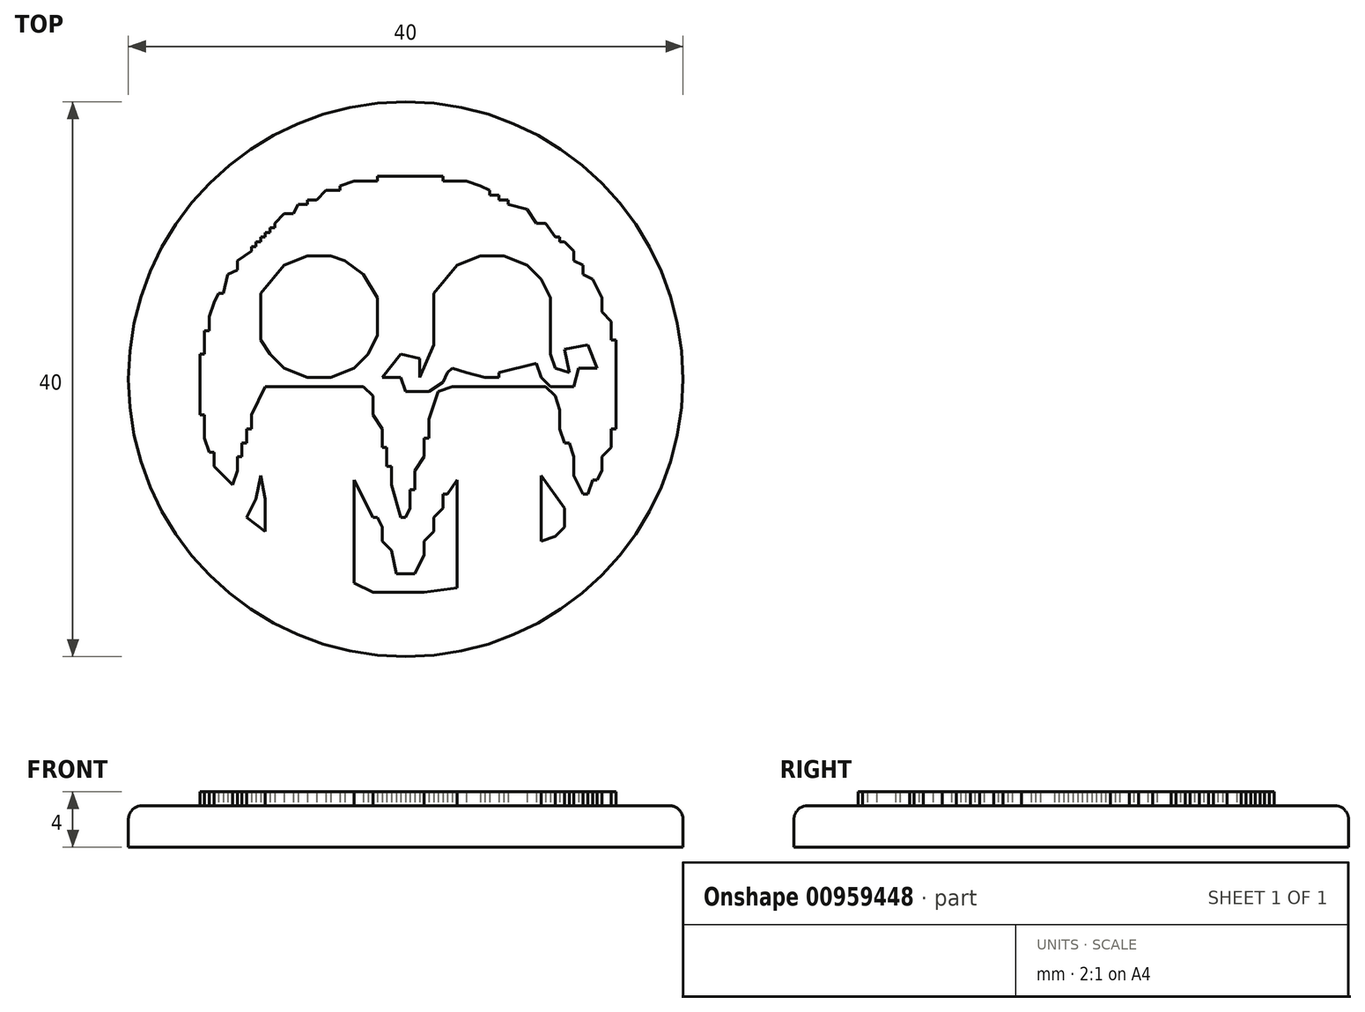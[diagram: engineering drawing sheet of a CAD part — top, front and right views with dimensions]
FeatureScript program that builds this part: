
annotation { "Feature Type Name" : "Feature", "Feature Type Description" : "" }
export const myFeature = defineFeature(function(context is Context, id is Id, definition is map)
    precondition{}
    {
        {
            var Q0;
            Q0=qCreatedBy(makeId("Front.planeOp"),FACE);
            var sketch = newSketch(context, id + "F0", { "sketchPlane" : qUnion([Q0])});
            skLineSegment(sketch, "E0.bottom", {"start": v(-20, 0) * mm, "end": v(0, 0) * mm});
            skLineSegment(sketch, "E0.top", {"start": v(-20, 3) * mm, "end": v(0, 3) * mm});
            skLineSegment(sketch, "E0.left", {"start": v(-20, 0) * mm, "end": v(-20, 3) * mm});
            skLineSegment(sketch, "E0.right", {"start": v(0, 0) * mm, "end": v(0, 3) * mm});
            skSolve(sketch);
        }
        {
            var Q0;
            Q0 = qSketchRegion(id + "F0", true);
            var Q1;
            Q1=sQuery(id+"F0.wireOp",EDGE,"E0.right");
            revolve(context, id + "F1", {"surfaceOperationType" : NewSurfaceOperationType.NEW, "entities" : qUnion([Q0]), "axis" : qUnion([Q1]), "revolveType" : RevolveType.FULL});
        }
        {
            var Q0;
            Q0=qCreatedBy(makeId("Top.planeOp"),FACE);
            cPlane(context, id + "F2", {"entities" : qUnion([Q0]), "cplaneType" : CPlaneType.OFFSET, "offset" : 3 * mm, "width" : 150 * mm, "height" : 150 * mm});
        }
        {
            var Q0;
            Q0=qCreatedBy(id+"F2.planeOp",FACE);
            var sketch = newSketch(context, id + "F3", { "sketchPlane" : qUnion([Q0])});
            skLineSegment(sketch, "E1", {"start": v(-2.03, 14.62) * mm, "end": v(-2.03, 14.29) * mm});
            skLineSegment(sketch, "E2", {"start": v(-2.03, 14.29) * mm, "end": v(-3.72, 14.29) * mm});
            skLineSegment(sketch, "E3", {"start": v(-3.72, 14.29) * mm, "end": v(-4.73, 13.95) * mm});
            skLineSegment(sketch, "E4", {"start": v(-4.73, 13.95) * mm, "end": v(-4.73, 13.61) * mm});
            skLineSegment(sketch, "E5", {"start": v(-4.73, 13.61) * mm, "end": v(-5.74, 13.61) * mm});
            skLineSegment(sketch, "E6", {"start": v(-5.74, 13.61) * mm, "end": v(-6.42, 12.94) * mm});
            skLineSegment(sketch, "E7", {"start": v(-6.42, 12.94) * mm, "end": v(-7.09, 12.94) * mm});
            skLineSegment(sketch, "E8", {"start": v(-7.09, 12.94) * mm, "end": v(-7.09, 12.6) * mm});
            skLineSegment(sketch, "E9", {"start": v(-7.09, 12.6) * mm, "end": v(-7.76, 12.6) * mm});
            skLineSegment(sketch, "E10", {"start": v(-7.76, 12.6) * mm, "end": v(-8.1, 11.93) * mm});
            skLineSegment(sketch, "E11", {"start": v(-8.1, 11.93) * mm, "end": v(-8.78, 11.93) * mm});
            skLineSegment(sketch, "E12", {"start": v(-8.78, 11.93) * mm, "end": v(-9.45, 11.25) * mm});
            skLineSegment(sketch, "E13", {"start": v(-9.45, 11.25) * mm, "end": v(-9.45, 10.92) * mm});
            skLineSegment(sketch, "E14", {"start": v(-9.45, 10.92) * mm, "end": v(-9.79, 10.92) * mm});
            skLineSegment(sketch, "E15", {"start": v(-9.79, 10.92) * mm, "end": v(-9.79, 10.58) * mm});
            skLineSegment(sketch, "E16", {"start": v(-9.79, 10.58) * mm, "end": v(-10.12, 10.58) * mm});
            skLineSegment(sketch, "E17", {"start": v(-10.12, 10.58) * mm, "end": v(-10.12, 10.24) * mm});
            skLineSegment(sketch, "E18", {"start": v(-10.12, 10.24) * mm, "end": v(-10.46, 10.24) * mm});
            skLineSegment(sketch, "E19", {"start": v(-10.46, 10.24) * mm, "end": v(-10.46, 9.9) * mm});
            skLineSegment(sketch, "E20", {"start": v(-10.46, 9.9) * mm, "end": v(-10.8, 9.9) * mm});
            skLineSegment(sketch, "E21", {"start": v(-10.8, 9.9) * mm, "end": v(-10.8, 9.57) * mm});
            skLineSegment(sketch, "E22", {"start": v(-10.8, 9.57) * mm, "end": v(-11.13, 9.57) * mm});
            skLineSegment(sketch, "E23", {"start": v(-11.13, 9.57) * mm, "end": v(-11.13, 9.23) * mm});
            skLineSegment(sketch, "E24", {"start": v(-11.13, 9.23) * mm, "end": v(-12.15, 8.56) * mm});
            skLineSegment(sketch, "E25", {"start": v(-12.15, 8.56) * mm, "end": v(-12.15, 7.88) * mm});
            skLineSegment(sketch, "E26", {"start": v(-12.15, 7.88) * mm, "end": v(-12.82, 7.54) * mm});
            skLineSegment(sketch, "E27", {"start": v(-12.82, 7.54) * mm, "end": v(-13.16, 6.2) * mm});
            skLineSegment(sketch, "E28", {"start": v(-13.16, 6.2) * mm, "end": v(-13.5, 6.2) * mm});
            skLineSegment(sketch, "E29", {"start": v(-13.5, 6.2) * mm, "end": v(-13.83, 5.52) * mm});
            skLineSegment(sketch, "E30", {"start": v(-13.83, 5.52) * mm, "end": v(-14.17, 4.51) * mm});
            skLineSegment(sketch, "E31", {"start": v(-14.17, 4.51) * mm, "end": v(-14.17, 3.5) * mm});
            skLineSegment(sketch, "E32", {"start": v(-14.17, 3.5) * mm, "end": v(-14.5, 3.5) * mm});
            skLineSegment(sketch, "E33", {"start": v(-14.5, 3.5) * mm, "end": v(-14.5, 1.81) * mm});
            skLineSegment(sketch, "E34", {"start": v(-14.5, 1.81) * mm, "end": v(-14.84, 1.81) * mm});
            skLineSegment(sketch, "E35", {"start": v(-14.84, 1.81) * mm, "end": v(-14.84, 0.8) * mm});
            skLineSegment(sketch, "E36", {"start": v(-14.84, 0.8) * mm, "end": v(-14.84, -2.57) * mm});
            skLineSegment(sketch, "E37", {"start": v(-14.84, -2.57) * mm, "end": v(-14.5, -2.57) * mm});
            skLineSegment(sketch, "E38", {"start": v(-14.5, -2.57) * mm, "end": v(-14.5, -4.25) * mm});
            skLineSegment(sketch, "E39", {"start": v(-14.5, -4.25) * mm, "end": v(-14.17, -5.26) * mm});
            skLineSegment(sketch, "E40", {"start": v(-14.17, -5.26) * mm, "end": v(-13.83, -5.26) * mm});
            skLineSegment(sketch, "E41", {"start": v(-13.83, -5.26) * mm, "end": v(-13.83, -6.28) * mm});
            skLineSegment(sketch, "E42", {"start": v(-13.83, -6.28) * mm, "end": v(-12.48, -7.62) * mm});
            skLineSegment(sketch, "E43", {"start": v(-12.48, -7.62) * mm, "end": v(-12.15, -6.61) * mm});
            skLineSegment(sketch, "E44", {"start": v(-12.15, -6.61) * mm, "end": v(-12.15, -5.6) * mm});
            skLineSegment(sketch, "E45", {"start": v(-12.15, -5.6) * mm, "end": v(-11.8, -5.6) * mm});
            skLineSegment(sketch, "E46", {"start": v(-11.8, -5.6) * mm, "end": v(-11.8, -4.59) * mm});
            skLineSegment(sketch, "E47", {"start": v(-11.8, -4.59) * mm, "end": v(-11.47, -4.59) * mm});
            skLineSegment(sketch, "E48", {"start": v(-11.47, -4.59) * mm, "end": v(-11.47, -3.58) * mm});
            skLineSegment(sketch, "E49", {"start": v(-11.47, -3.58) * mm, "end": v(-11.13, -3.58) * mm});
            skLineSegment(sketch, "E50", {"start": v(-11.13, -3.58) * mm, "end": v(-11.13, -2.57) * mm});
            skLineSegment(sketch, "E51", {"start": v(-11.13, -2.57) * mm, "end": v(-10.12, -0.55) * mm});
            skLineSegment(sketch, "E52", {"start": v(-10.12, -0.55) * mm, "end": v(-8.78, -0.55) * mm});
            skLineSegment(sketch, "E53", {"start": v(-8.78, -0.55) * mm, "end": v(-8.44, -0.55) * mm});
            skLineSegment(sketch, "E54", {"start": v(-8.44, -0.55) * mm, "end": v(-8.1, -0.55) * mm});
            skLineSegment(sketch, "E55", {"start": v(-8.1, -0.55) * mm, "end": v(-7.76, -0.55) * mm});
            skLineSegment(sketch, "E56", {"start": v(-7.76, -0.55) * mm, "end": v(-7.43, -0.55) * mm});
            skLineSegment(sketch, "E57", {"start": v(-7.43, -0.55) * mm, "end": v(-7.09, -0.55) * mm});
            skLineSegment(sketch, "E58", {"start": v(-7.09, -0.55) * mm, "end": v(-6.75, -0.55) * mm});
            skLineSegment(sketch, "E59", {"start": v(-6.75, -0.55) * mm, "end": v(-6.42, -0.55) * mm});
            skLineSegment(sketch, "E60", {"start": v(-6.42, -0.55) * mm, "end": v(-6.08, -0.55) * mm});
            skLineSegment(sketch, "E61", {"start": v(-6.08, -0.55) * mm, "end": v(-5.74, -0.55) * mm});
            skLineSegment(sketch, "E62", {"start": v(-5.74, -0.55) * mm, "end": v(-5.4, -0.55) * mm});
            skLineSegment(sketch, "E63", {"start": v(-5.4, -0.55) * mm, "end": v(-5.07, -0.55) * mm});
            skLineSegment(sketch, "E64", {"start": v(-5.07, -0.55) * mm, "end": v(-3.04, -0.55) * mm});
            skLineSegment(sketch, "E65", {"start": v(-3.04, -0.55) * mm, "end": v(-2.37, -1.22) * mm});
            skLineSegment(sketch, "E66", {"start": v(-2.37, -1.22) * mm, "end": v(-2.37, -2.57) * mm});
            skLineSegment(sketch, "E67", {"start": v(-2.37, -2.57) * mm, "end": v(-1.7, -3.58) * mm});
            skLineSegment(sketch, "E68", {"start": v(-1.7, -3.58) * mm, "end": v(-1.7, -4.93) * mm});
            skLineSegment(sketch, "E69", {"start": v(-1.7, -4.93) * mm, "end": v(-1.36, -4.93) * mm});
            skLineSegment(sketch, "E70", {"start": v(-1.36, -4.93) * mm, "end": v(-1.36, -6.28) * mm});
            skLineSegment(sketch, "E71", {"start": v(-1.36, -6.28) * mm, "end": v(-1.02, -6.28) * mm});
            skLineSegment(sketch, "E72", {"start": v(-1.02, -6.28) * mm, "end": v(-1.02, -7.62) * mm});
            skLineSegment(sketch, "E73", {"start": v(-1.02, -7.62) * mm, "end": v(-0.35, -9.98) * mm});
            skLineSegment(sketch, "E74", {"start": v(-0.35, -9.98) * mm, "end": v(-0.01, -9.98) * mm});
            skLineSegment(sketch, "E75", {"start": v(-0.01, -9.98) * mm, "end": v(0.33, -9.3) * mm});
            skLineSegment(sketch, "E76", {"start": v(0.33, -9.3) * mm, "end": v(0.33, -7.96) * mm});
            skLineSegment(sketch, "E77", {"start": v(0.33, -7.96) * mm, "end": v(0.66, -7.96) * mm});
            skLineSegment(sketch, "E78", {"start": v(0.66, -7.96) * mm, "end": v(0.66, -6.61) * mm});
            skLineSegment(sketch, "E79", {"start": v(0.66, -6.61) * mm, "end": v(1.34, -5.6) * mm});
            skLineSegment(sketch, "E80", {"start": v(1.34, -5.6) * mm, "end": v(1.34, -4.25) * mm});
            skLineSegment(sketch, "E81", {"start": v(1.34, -4.25) * mm, "end": v(1.67, -4.25) * mm});
            skLineSegment(sketch, "E82", {"start": v(1.67, -4.25) * mm, "end": v(1.67, -2.9) * mm});
            skLineSegment(sketch, "E83", {"start": v(1.67, -2.9) * mm, "end": v(2.35, -0.88) * mm});
            skLineSegment(sketch, "E84", {"start": v(2.35, -0.88) * mm, "end": v(3.36, -0.55) * mm});
            skLineSegment(sketch, "E85", {"start": v(3.36, -0.55) * mm, "end": v(4.7, -0.55) * mm});
            skLineSegment(sketch, "E86", {"start": v(4.7, -0.55) * mm, "end": v(5.04, -0.55) * mm});
            skLineSegment(sketch, "E87", {"start": v(5.04, -0.55) * mm, "end": v(5.38, -0.55) * mm});
            skLineSegment(sketch, "E88", {"start": v(5.38, -0.55) * mm, "end": v(5.72, -0.55) * mm});
            skLineSegment(sketch, "E89", {"start": v(5.72, -0.55) * mm, "end": v(6.06, -0.55) * mm});
            skLineSegment(sketch, "E90", {"start": v(6.06, -0.55) * mm, "end": v(6.4, -0.55) * mm});
            skLineSegment(sketch, "E91", {"start": v(6.4, -0.55) * mm, "end": v(6.73, -0.55) * mm});
            skLineSegment(sketch, "E92", {"start": v(6.73, -0.55) * mm, "end": v(7.07, -0.55) * mm});
            skLineSegment(sketch, "E93", {"start": v(7.07, -0.55) * mm, "end": v(7.4, -0.55) * mm});
            skLineSegment(sketch, "E94", {"start": v(7.4, -0.55) * mm, "end": v(7.74, -0.55) * mm});
            skLineSegment(sketch, "E95", {"start": v(7.74, -0.55) * mm, "end": v(8.08, -0.55) * mm});
            skLineSegment(sketch, "E96", {"start": v(8.08, -0.55) * mm, "end": v(8.42, -0.55) * mm});
            skLineSegment(sketch, "E97", {"start": v(8.42, -0.55) * mm, "end": v(10.1, -0.55) * mm});
            skLineSegment(sketch, "E98", {"start": v(10.1, -0.55) * mm, "end": v(10.78, -1.22) * mm});
            skLineSegment(sketch, "E99", {"start": v(10.78, -1.22) * mm, "end": v(11.11, -2.23) * mm});
            skLineSegment(sketch, "E100", {"start": v(11.11, -2.23) * mm, "end": v(11.11, -3.58) * mm});
            skLineSegment(sketch, "E101", {"start": v(11.11, -3.58) * mm, "end": v(11.45, -4.59) * mm});
            skLineSegment(sketch, "E102", {"start": v(11.45, -4.59) * mm, "end": v(11.79, -4.59) * mm});
            skLineSegment(sketch, "E103", {"start": v(11.79, -4.59) * mm, "end": v(12.12, -5.6) * mm});
            skLineSegment(sketch, "E104", {"start": v(12.12, -5.6) * mm, "end": v(12.12, -6.95) * mm});
            skLineSegment(sketch, "E105", {"start": v(12.12, -6.95) * mm, "end": v(12.8, -8.3) * mm});
            skLineSegment(sketch, "E106", {"start": v(12.8, -8.3) * mm, "end": v(13.13, -8.3) * mm});
            skLineSegment(sketch, "E107", {"start": v(13.13, -8.3) * mm, "end": v(13.47, -7.29) * mm});
            skLineSegment(sketch, "E108", {"start": v(13.47, -7.29) * mm, "end": v(13.8, -7.29) * mm});
            skLineSegment(sketch, "E109", {"start": v(13.8, -7.29) * mm, "end": v(14.15, -6.61) * mm});
            skLineSegment(sketch, "E110", {"start": v(14.15, -6.61) * mm, "end": v(14.15, -5.6) * mm});
            skLineSegment(sketch, "E111", {"start": v(14.15, -5.6) * mm, "end": v(14.82, -4.93) * mm});
            skLineSegment(sketch, "E112", {"start": v(14.82, -4.93) * mm, "end": v(14.82, -3.58) * mm});
            skLineSegment(sketch, "E113", {"start": v(14.82, -3.58) * mm, "end": v(15.16, -3.58) * mm});
            skLineSegment(sketch, "E114", {"start": v(15.16, -3.58) * mm, "end": v(15.16, -2.57) * mm});
            skLineSegment(sketch, "E115", {"start": v(15.16, -2.57) * mm, "end": v(15.16, -1.22) * mm});
            skLineSegment(sketch, "E116", {"start": v(15.16, -1.22) * mm, "end": v(15.16, -0.88) * mm});
            skLineSegment(sketch, "E117", {"start": v(15.16, -0.88) * mm, "end": v(15.16, -0.55) * mm});
            skLineSegment(sketch, "E118", {"start": v(15.16, -0.55) * mm, "end": v(15.16, -0.2) * mm});
            skLineSegment(sketch, "E119", {"start": v(15.16, -0.2) * mm, "end": v(15.16, 0.13) * mm});
            skLineSegment(sketch, "E120", {"start": v(15.16, 0.13) * mm, "end": v(15.16, 0.47) * mm});
            skLineSegment(sketch, "E121", {"start": v(15.16, 0.47) * mm, "end": v(15.16, 0.8) * mm});
            skLineSegment(sketch, "E122", {"start": v(15.16, 0.8) * mm, "end": v(15.16, 1.14) * mm});
            skLineSegment(sketch, "E123", {"start": v(15.16, 1.14) * mm, "end": v(15.16, 2.83) * mm});
            skLineSegment(sketch, "E124", {"start": v(15.16, 2.83) * mm, "end": v(14.82, 2.83) * mm});
            skLineSegment(sketch, "E125", {"start": v(14.82, 2.83) * mm, "end": v(14.82, 4.17) * mm});
            skLineSegment(sketch, "E126", {"start": v(14.82, 4.17) * mm, "end": v(14.15, 4.85) * mm});
            skLineSegment(sketch, "E127", {"start": v(14.15, 4.85) * mm, "end": v(14.15, 5.86) * mm});
            skLineSegment(sketch, "E128", {"start": v(14.15, 5.86) * mm, "end": v(13.47, 7.2) * mm});
            skLineSegment(sketch, "E129", {"start": v(13.47, 7.2) * mm, "end": v(12.8, 7.54) * mm});
            skLineSegment(sketch, "E130", {"start": v(12.8, 7.54) * mm, "end": v(12.8, 8.22) * mm});
            skLineSegment(sketch, "E131", {"start": v(12.8, 8.22) * mm, "end": v(12.12, 8.56) * mm});
            skLineSegment(sketch, "E132", {"start": v(12.12, 8.56) * mm, "end": v(12.12, 9.23) * mm});
            skLineSegment(sketch, "E133", {"start": v(12.12, 9.23) * mm, "end": v(11.45, 9.9) * mm});
            skLineSegment(sketch, "E134", {"start": v(11.45, 9.9) * mm, "end": v(11.11, 9.9) * mm});
            skLineSegment(sketch, "E135", {"start": v(11.11, 9.9) * mm, "end": v(11.11, 10.24) * mm});
            skLineSegment(sketch, "E136", {"start": v(11.11, 10.24) * mm, "end": v(10.78, 10.24) * mm});
            skLineSegment(sketch, "E137", {"start": v(10.78, 10.24) * mm, "end": v(10.1, 11.25) * mm});
            skLineSegment(sketch, "E138", {"start": v(10.1, 11.25) * mm, "end": v(9.43, 11.25) * mm});
            skLineSegment(sketch, "E139", {"start": v(9.43, 11.25) * mm, "end": v(8.75, 12.26) * mm});
            skLineSegment(sketch, "E140", {"start": v(8.75, 12.26) * mm, "end": v(7.4, 12.6) * mm});
            skLineSegment(sketch, "E141", {"start": v(7.4, 12.6) * mm, "end": v(7.4, 12.94) * mm});
            skLineSegment(sketch, "E142", {"start": v(7.4, 12.94) * mm, "end": v(6.73, 12.94) * mm});
            skLineSegment(sketch, "E143", {"start": v(6.73, 12.94) * mm, "end": v(6.73, 13.28) * mm});
            skLineSegment(sketch, "E144", {"start": v(6.73, 13.28) * mm, "end": v(6.06, 13.28) * mm});
            skLineSegment(sketch, "E145", {"start": v(6.06, 13.28) * mm, "end": v(6.06, 13.61) * mm});
            skLineSegment(sketch, "E146", {"start": v(6.06, 13.61) * mm, "end": v(5.38, 13.95) * mm});
            skLineSegment(sketch, "E147", {"start": v(5.38, 13.95) * mm, "end": v(4.37, 14.29) * mm});
            skLineSegment(sketch, "E148", {"start": v(4.37, 14.29) * mm, "end": v(2.69, 14.29) * mm});
            skLineSegment(sketch, "E149", {"start": v(2.69, 14.29) * mm, "end": v(2.69, 14.62) * mm});
            skLineSegment(sketch, "E150", {"start": v(2.69, 14.62) * mm, "end": v(1.67, 14.62) * mm});
            skLineSegment(sketch, "E151", {"start": v(1.67, 14.62) * mm, "end": v(0.33, 14.62) * mm});
            skLineSegment(sketch, "E152", {"start": v(0.33, 14.62) * mm, "end": v(-0.01, 14.62) * mm});
            skLineSegment(sketch, "E153", {"start": v(-0.01, 14.62) * mm, "end": v(-0.35, 14.62) * mm});
            skLineSegment(sketch, "E154", {"start": v(-0.35, 14.62) * mm, "end": v(-0.69, 14.62) * mm});
            skLineSegment(sketch, "E155", {"start": v(-0.69, 14.62) * mm, "end": v(-2.03, 14.62) * mm});
            skLineSegment(sketch, "E156", {"start": v(-7.09, 8.9) * mm, "end": v(-8.78, 8.22) * mm});
            skLineSegment(sketch, "E157", {"start": v(-8.78, 8.22) * mm, "end": v(-10.46, 6.2) * mm});
            skLineSegment(sketch, "E158", {"start": v(-10.46, 6.2) * mm, "end": v(-10.46, 2.83) * mm});
            skLineSegment(sketch, "E159", {"start": v(-10.46, 2.83) * mm, "end": v(-9.79, 1.81) * mm});
            skLineSegment(sketch, "E160", {"start": v(-9.79, 1.81) * mm, "end": v(-8.78, 0.8) * mm});
            skLineSegment(sketch, "E161", {"start": v(-8.78, 0.8) * mm, "end": v(-7.09, 0.13) * mm});
            skLineSegment(sketch, "E162", {"start": v(-7.09, 0.13) * mm, "end": v(-5.4, 0.13) * mm});
            skLineSegment(sketch, "E163", {"start": v(-5.4, 0.13) * mm, "end": v(-3.72, 0.8) * mm});
            skLineSegment(sketch, "E164", {"start": v(-3.72, 0.8) * mm, "end": v(-2.7, 1.81) * mm});
            skLineSegment(sketch, "E165", {"start": v(-2.7, 1.81) * mm, "end": v(-2.03, 3.16) * mm});
            skLineSegment(sketch, "E166", {"start": v(-2.03, 3.16) * mm, "end": v(-2.03, 5.86) * mm});
            skLineSegment(sketch, "E167", {"start": v(-2.03, 5.86) * mm, "end": v(-3.04, 7.54) * mm});
            skLineSegment(sketch, "E168", {"start": v(-3.04, 7.54) * mm, "end": v(-4.4, 8.56) * mm});
            skLineSegment(sketch, "E169", {"start": v(-4.4, 8.56) * mm, "end": v(-5.4, 8.9) * mm});
            skLineSegment(sketch, "E170", {"start": v(-5.4, 8.9) * mm, "end": v(-7.09, 8.9) * mm});
            skLineSegment(sketch, "E171", {"start": v(5.38, 8.9) * mm, "end": v(3.7, 8.22) * mm});
            skLineSegment(sketch, "E172", {"start": v(3.7, 8.22) * mm, "end": v(2.01, 6.2) * mm});
            skLineSegment(sketch, "E173", {"start": v(2.01, 6.2) * mm, "end": v(2.01, 4.85) * mm});
            skLineSegment(sketch, "E174", {"start": v(2.01, 4.85) * mm, "end": v(2.01, 4.51) * mm});
            skLineSegment(sketch, "E175", {"start": v(2.01, 4.51) * mm, "end": v(2.01, 4.17) * mm});
            skLineSegment(sketch, "E176", {"start": v(2.01, 4.17) * mm, "end": v(2.01, 3.84) * mm});
            skLineSegment(sketch, "E177", {"start": v(2.01, 3.84) * mm, "end": v(2.01, 3.5) * mm});
            skLineSegment(sketch, "E178", {"start": v(2.01, 3.5) * mm, "end": v(2.01, 3.16) * mm});
            skLineSegment(sketch, "E179", {"start": v(2.01, 3.16) * mm, "end": v(2.01, 2.83) * mm});
            skLineSegment(sketch, "E180", {"start": v(2.01, 2.83) * mm, "end": v(2.01, 2.49) * mm});
            skLineSegment(sketch, "E181", {"start": v(2.01, 2.49) * mm, "end": v(1, 0.13) * mm});
            skLineSegment(sketch, "E182", {"start": v(1, 0.13) * mm, "end": v(1, 1.48) * mm});
            skLineSegment(sketch, "E183", {"start": v(1, 1.48) * mm, "end": v(-0.35, 1.81) * mm});
            skLineSegment(sketch, "E184", {"start": v(-0.35, 1.81) * mm, "end": v(-1.7, 0.13) * mm});
            skLineSegment(sketch, "E185", {"start": v(-1.7, 0.13) * mm, "end": v(-0.35, 0.13) * mm});
            skLineSegment(sketch, "E186", {"start": v(-0.35, 0.13) * mm, "end": v(-0.01, -0.88) * mm});
            skLineSegment(sketch, "E187", {"start": v(-0.01, -0.88) * mm, "end": v(1.67, -0.88) * mm});
            skLineSegment(sketch, "E188", {"start": v(1.67, -0.88) * mm, "end": v(2.69, -0.2) * mm});
            skLineSegment(sketch, "E189", {"start": v(2.69, -0.2) * mm, "end": v(3.02, 0.47) * mm});
            skLineSegment(sketch, "E190", {"start": v(3.02, 0.47) * mm, "end": v(3.36, 0.8) * mm});
            skLineSegment(sketch, "E191", {"start": v(3.36, 0.8) * mm, "end": v(4.37, 0.47) * mm});
            skLineSegment(sketch, "E192", {"start": v(4.37, 0.47) * mm, "end": v(5.72, 0.13) * mm});
            skLineSegment(sketch, "E193", {"start": v(5.72, 0.13) * mm, "end": v(6.73, 0.13) * mm});
            skLineSegment(sketch, "E194", {"start": v(6.73, 0.13) * mm, "end": v(6.73, 0.47) * mm});
            skLineSegment(sketch, "E195", {"start": v(6.73, 0.47) * mm, "end": v(9.43, 1.14) * mm});
            skLineSegment(sketch, "E196", {"start": v(9.43, 1.14) * mm, "end": v(9.76, 0.13) * mm});
            skLineSegment(sketch, "E197", {"start": v(9.76, 0.13) * mm, "end": v(10.1, -0.2) * mm});
            skLineSegment(sketch, "E198", {"start": v(10.1, -0.2) * mm, "end": v(10.44, -0.55) * mm});
            skLineSegment(sketch, "E199", {"start": v(10.44, -0.55) * mm, "end": v(12.12, -0.55) * mm});
            skLineSegment(sketch, "E200", {"start": v(12.12, -0.55) * mm, "end": v(12.46, 0.8) * mm});
            skLineSegment(sketch, "E201", {"start": v(12.46, 0.8) * mm, "end": v(13.8, 0.8) * mm});
            skLineSegment(sketch, "E202", {"start": v(13.8, 0.8) * mm, "end": v(13.13, 2.49) * mm});
            skLineSegment(sketch, "E203", {"start": v(13.13, 2.49) * mm, "end": v(11.45, 2.15) * mm});
            skLineSegment(sketch, "E204", {"start": v(11.45, 2.15) * mm, "end": v(11.79, 0.47) * mm});
            skLineSegment(sketch, "E205", {"start": v(11.79, 0.47) * mm, "end": v(10.78, 0.8) * mm});
            skLineSegment(sketch, "E206", {"start": v(10.78, 0.8) * mm, "end": v(10.44, 1.81) * mm});
            skLineSegment(sketch, "E207", {"start": v(10.44, 1.81) * mm, "end": v(10.44, 3.16) * mm});
            skLineSegment(sketch, "E208", {"start": v(10.44, 3.16) * mm, "end": v(10.44, 3.5) * mm});
            skLineSegment(sketch, "E209", {"start": v(10.44, 3.5) * mm, "end": v(10.44, 3.84) * mm});
            skLineSegment(sketch, "E210", {"start": v(10.44, 3.84) * mm, "end": v(10.44, 4.17) * mm});
            skLineSegment(sketch, "E211", {"start": v(10.44, 4.17) * mm, "end": v(10.44, 5.86) * mm});
            skLineSegment(sketch, "E212", {"start": v(10.44, 5.86) * mm, "end": v(9.76, 7.2) * mm});
            skLineSegment(sketch, "E213", {"start": v(9.76, 7.2) * mm, "end": v(8.75, 8.22) * mm});
            skLineSegment(sketch, "E214", {"start": v(8.75, 8.22) * mm, "end": v(7.07, 8.9) * mm});
            skLineSegment(sketch, "E215", {"start": v(7.07, 8.9) * mm, "end": v(5.38, 8.9) * mm});
            skLineSegment(sketch, "E216", {"start": v(-10.46, -6.95) * mm, "end": v(-10.8, -8.63) * mm});
            skLineSegment(sketch, "E217", {"start": v(-10.8, -8.63) * mm, "end": v(-11.47, -9.98) * mm});
            skLineSegment(sketch, "E218", {"start": v(-11.47, -9.98) * mm, "end": v(-10.12, -11) * mm});
            skLineSegment(sketch, "E219", {"start": v(-10.12, -11) * mm, "end": v(-10.12, -9.65) * mm});
            skLineSegment(sketch, "E220", {"start": v(-10.12, -9.65) * mm, "end": v(-10.12, -9.3) * mm});
            skLineSegment(sketch, "E221", {"start": v(-10.12, -9.3) * mm, "end": v(-10.12, -8.97) * mm});
            skLineSegment(sketch, "E222", {"start": v(-10.12, -8.97) * mm, "end": v(-10.12, -8.63) * mm});
            skLineSegment(sketch, "E223", {"start": v(-10.12, -8.63) * mm, "end": v(-10.46, -6.95) * mm});
            skLineSegment(sketch, "E224", {"start": v(9.76, -6.95) * mm, "end": v(9.76, -8.3) * mm});
            skLineSegment(sketch, "E225", {"start": v(9.76, -8.3) * mm, "end": v(9.76, -8.63) * mm});
            skLineSegment(sketch, "E226", {"start": v(9.76, -8.63) * mm, "end": v(9.76, -8.97) * mm});
            skLineSegment(sketch, "E227", {"start": v(9.76, -8.97) * mm, "end": v(9.76, -9.3) * mm});
            skLineSegment(sketch, "E228", {"start": v(9.76, -9.3) * mm, "end": v(9.76, -11.67) * mm});
            skLineSegment(sketch, "E229", {"start": v(9.76, -11.67) * mm, "end": v(10.78, -11.33) * mm});
            skLineSegment(sketch, "E230", {"start": v(10.78, -11.33) * mm, "end": v(11.11, -11) * mm});
            skLineSegment(sketch, "E231", {"start": v(11.11, -11) * mm, "end": v(11.45, -10.66) * mm});
            skLineSegment(sketch, "E232", {"start": v(11.45, -10.66) * mm, "end": v(11.45, -9.3) * mm});
            skLineSegment(sketch, "E233", {"start": v(11.45, -9.3) * mm, "end": v(9.76, -6.95) * mm});
            skLineSegment(sketch, "E234", {"start": v(-3.72, -7.29) * mm, "end": v(-3.72, -8.63) * mm});
            skLineSegment(sketch, "E235", {"start": v(-3.72, -8.63) * mm, "end": v(-3.72, -8.97) * mm});
            skLineSegment(sketch, "E236", {"start": v(-3.72, -8.97) * mm, "end": v(-3.72, -9.3) * mm});
            skLineSegment(sketch, "E237", {"start": v(-3.72, -9.3) * mm, "end": v(-3.72, -9.65) * mm});
            skLineSegment(sketch, "E238", {"start": v(-3.72, -9.65) * mm, "end": v(-3.72, -9.98) * mm});
            skLineSegment(sketch, "E239", {"start": v(-3.72, -9.98) * mm, "end": v(-3.72, -10.32) * mm});
            skLineSegment(sketch, "E240", {"start": v(-3.72, -10.32) * mm, "end": v(-3.72, -10.66) * mm});
            skLineSegment(sketch, "E241", {"start": v(-3.72, -10.66) * mm, "end": v(-3.72, -11) * mm});
            skLineSegment(sketch, "E242", {"start": v(-3.72, -11) * mm, "end": v(-3.72, -11.33) * mm});
            skLineSegment(sketch, "E243", {"start": v(-3.72, -11.33) * mm, "end": v(-3.72, -11.67) * mm});
            skLineSegment(sketch, "E244", {"start": v(-3.72, -11.67) * mm, "end": v(-3.72, -12) * mm});
            skLineSegment(sketch, "E245", {"start": v(-3.72, -12) * mm, "end": v(-3.72, -12.34) * mm});
            skLineSegment(sketch, "E246", {"start": v(-3.72, -12.34) * mm, "end": v(-3.72, -14.7) * mm});
            skLineSegment(sketch, "E247", {"start": v(-3.72, -14.7) * mm, "end": v(-2.37, -15.38) * mm});
            skLineSegment(sketch, "E248", {"start": v(-2.37, -15.38) * mm, "end": v(-1.02, -15.38) * mm});
            skLineSegment(sketch, "E249", {"start": v(-1.02, -15.38) * mm, "end": v(-0.69, -15.38) * mm});
            skLineSegment(sketch, "E250", {"start": v(-0.69, -15.38) * mm, "end": v(-0.35, -15.38) * mm});
            skLineSegment(sketch, "E251", {"start": v(-0.35, -15.38) * mm, "end": v(-0.01, -15.38) * mm});
            skLineSegment(sketch, "E252", {"start": v(-0.01, -15.38) * mm, "end": v(0.33, -15.38) * mm});
            skLineSegment(sketch, "E253", {"start": v(0.33, -15.38) * mm, "end": v(0.66, -15.38) * mm});
            skLineSegment(sketch, "E254", {"start": v(0.66, -15.38) * mm, "end": v(1, -15.38) * mm});
            skLineSegment(sketch, "E255", {"start": v(1, -15.38) * mm, "end": v(1.34, -15.38) * mm});
            skLineSegment(sketch, "E256", {"start": v(1.34, -15.38) * mm, "end": v(3.7, -15.04) * mm});
            skLineSegment(sketch, "E257", {"start": v(3.7, -15.04) * mm, "end": v(3.7, -13.7) * mm});
            skLineSegment(sketch, "E258", {"start": v(3.7, -13.7) * mm, "end": v(3.7, -13.35) * mm});
            skLineSegment(sketch, "E259", {"start": v(3.7, -13.35) * mm, "end": v(3.7, -13.02) * mm});
            skLineSegment(sketch, "E260", {"start": v(3.7, -13.02) * mm, "end": v(3.7, -12.68) * mm});
            skLineSegment(sketch, "E261", {"start": v(3.7, -12.68) * mm, "end": v(3.7, -12.34) * mm});
            skLineSegment(sketch, "E262", {"start": v(3.7, -12.34) * mm, "end": v(3.7, -12) * mm});
            skLineSegment(sketch, "E263", {"start": v(3.7, -12) * mm, "end": v(3.7, -11.67) * mm});
            skLineSegment(sketch, "E264", {"start": v(3.7, -11.67) * mm, "end": v(3.7, -11.33) * mm});
            skLineSegment(sketch, "E265", {"start": v(3.7, -11.33) * mm, "end": v(3.7, -11) * mm});
            skLineSegment(sketch, "E266", {"start": v(3.7, -11) * mm, "end": v(3.7, -10.66) * mm});
            skLineSegment(sketch, "E267", {"start": v(3.7, -10.66) * mm, "end": v(3.7, -10.32) * mm});
            skLineSegment(sketch, "E268", {"start": v(3.7, -10.32) * mm, "end": v(3.7, -9.98) * mm});
            skLineSegment(sketch, "E269", {"start": v(3.7, -9.98) * mm, "end": v(3.7, -9.65) * mm});
            skLineSegment(sketch, "E270", {"start": v(3.7, -9.65) * mm, "end": v(3.7, -9.3) * mm});
            skLineSegment(sketch, "E271", {"start": v(3.7, -9.3) * mm, "end": v(3.7, -8.97) * mm});
            skLineSegment(sketch, "E272", {"start": v(3.7, -8.97) * mm, "end": v(3.7, -8.63) * mm});
            skLineSegment(sketch, "E273", {"start": v(3.7, -8.63) * mm, "end": v(3.7, -7.29) * mm});
            skLineSegment(sketch, "E274", {"start": v(3.7, -7.29) * mm, "end": v(3.02, -8.3) * mm});
            skLineSegment(sketch, "E275", {"start": v(3.02, -8.3) * mm, "end": v(2.69, -8.3) * mm});
            skLineSegment(sketch, "E276", {"start": v(2.69, -8.3) * mm, "end": v(2.69, -9.3) * mm});
            skLineSegment(sketch, "E277", {"start": v(2.69, -9.3) * mm, "end": v(2.01, -9.98) * mm});
            skLineSegment(sketch, "E278", {"start": v(2.01, -9.98) * mm, "end": v(2.01, -11) * mm});
            skLineSegment(sketch, "E279", {"start": v(2.01, -11) * mm, "end": v(1.34, -11.67) * mm});
            skLineSegment(sketch, "E280", {"start": v(1.34, -11.67) * mm, "end": v(1.34, -12.68) * mm});
            skLineSegment(sketch, "E281", {"start": v(1.34, -12.68) * mm, "end": v(0.66, -14.03) * mm});
            skLineSegment(sketch, "E282", {"start": v(0.66, -14.03) * mm, "end": v(-0.69, -14.03) * mm});
            skLineSegment(sketch, "E283", {"start": v(-0.69, -14.03) * mm, "end": v(-1.02, -12.34) * mm});
            skLineSegment(sketch, "E284", {"start": v(-1.02, -12.34) * mm, "end": v(-1.7, -11.67) * mm});
            skLineSegment(sketch, "E285", {"start": v(-1.7, -11.67) * mm, "end": v(-1.7, -10.66) * mm});
            skLineSegment(sketch, "E286", {"start": v(-1.7, -10.66) * mm, "end": v(-2.03, -9.98) * mm});
            skLineSegment(sketch, "E287", {"start": v(-2.03, -9.98) * mm, "end": v(-2.37, -9.98) * mm});
            skLineSegment(sketch, "E288", {"start": v(-2.37, -9.98) * mm, "end": v(-2.7, -9.3) * mm});
            skLineSegment(sketch, "E289", {"start": v(-2.7, -9.3) * mm, "end": v(-3.72, -7.29) * mm});
            skSolve(sketch);
        }
        {
            var Q0;
            Q0 = qSketchRegion(id + "F3", true);
            extrude(context, id + "F4", {"entities" : qUnion([Q0]), "operationType" : NewBodyOperationType.ADD, "depth" : 1 * mm, "offsetDistance" : 25 * mm});
        }
        {
            var Q0;
            Q0=makeQuery(id+"F1.opRevolve","SWEPT_EDGE",EDGE,{"disambiguationData":[OSD([sQuery(id+"F0.wireOp",EDGE,"E0.top"),sQuery(id+"F0.wireOp",EDGE,"E0.left")])]});
            fillet(context, id + "F5", {"entities" : qUnion([Q0]), "radius" : 1 * mm, "tangentPropagation" : true, "allowEdgeOverflow" : false});
        }
    });
